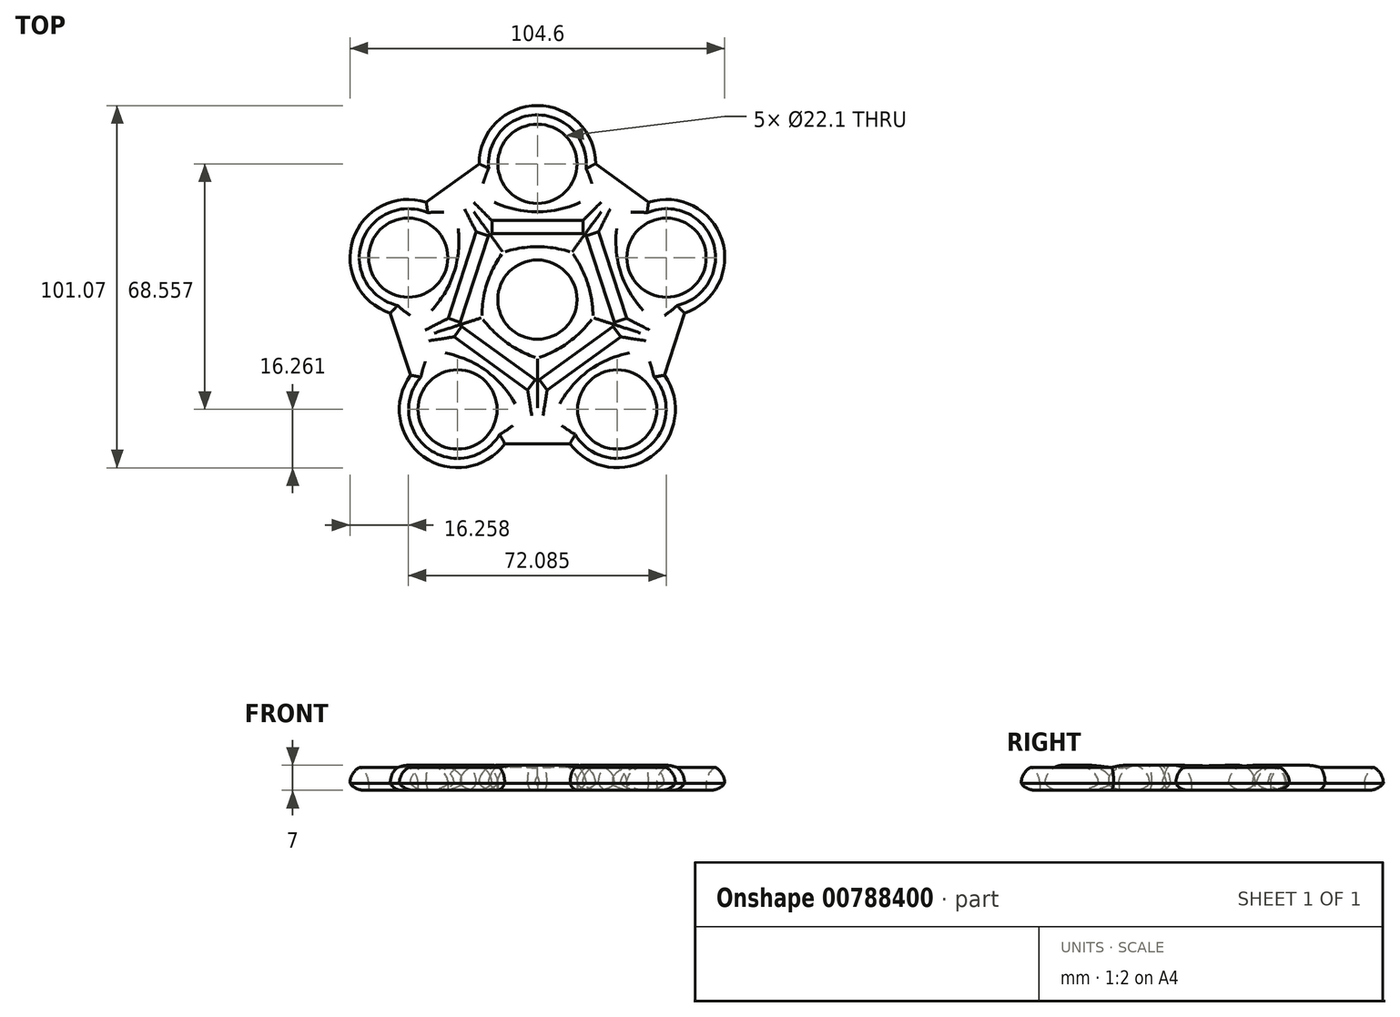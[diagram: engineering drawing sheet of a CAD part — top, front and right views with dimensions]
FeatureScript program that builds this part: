
annotation { "Feature Type Name" : "Feature", "Feature Type Description" : "" }
export const myFeature = defineFeature(function(context is Context, id is Id, definition is map)
    precondition{}
    {
        {
            var Q0;
            Q0=qCreatedBy(makeId("Top.planeOp"),FACE);
            var sketch = newSketch(context, id + "F0", { "sketchPlane" : qUnion([Q0])});
            skCircle(sketch, "E0", {"center": v(0, 0) * mm, "radius": 11.05 * mm});
            skCircle(sketch, "E1", {"center": v(0, 37.9) * mm, "radius": 11.05 * mm});
            skCircle(sketch, "E2.1.0", {"center": v(-36.04, 11.71) * mm, "radius": 11.05 * mm});
            skCircle(sketch, "E2.2.0", {"center": v(-22.28, -30.66) * mm, "radius": 11.05 * mm});
            skCircle(sketch, "E2.3.0", {"center": v(22.28, -30.66) * mm, "radius": 11.05 * mm});
            skCircle(sketch, "E2.4.0", {"center": v(36.04, 11.71) * mm, "radius": 11.05 * mm});
            skLineSegment(sketch, "E3", {"start": v(0, 37.9) * mm, "end": v(16.26, 37.9) * mm, "construction": true});
            skLineSegment(sketch, "E4", {"start": v(-16.26, 37.9) * mm, "end": v(-16.26, 37.9) * mm});
            skArc(sketch, "E5", {"start": v(16.26, 37.9) * mm, "mid": v(0, 54.15) * mm, "end": v(-16.26, 37.9) * mm});
            skArc(sketch, "E6.1.0", {"start": v(-31.02, 27.17) * mm, "mid": v(-51.5, 16.73) * mm, "end": v(-41.07, -3.75) * mm});
            skArc(sketch, "E6.2.0", {"start": v(-35.43, -21.1) * mm, "mid": v(-31.83, -43.81) * mm, "end": v(-9.12, -40.21) * mm});
            skArc(sketch, "E6.3.0", {"start": v(9.12, -40.21) * mm, "mid": v(31.83, -43.81) * mm, "end": v(35.43, -21.1) * mm});
            skArc(sketch, "E6.4.0", {"start": v(41.07, -3.75) * mm, "mid": v(51.5, 16.73) * mm, "end": v(31.02, 27.17) * mm});
            skLineSegment(sketch, "E7", {"start": v(-16.26, 37.9) * mm, "end": v(-31.02, 27.17) * mm});
            skLineSegment(sketch, "E8.1.0", {"start": v(-41.07, -3.75) * mm, "end": v(-35.43, -21.1) * mm});
            skLineSegment(sketch, "E8.2.0", {"start": v(-9.12, -40.21) * mm, "end": v(9.12, -40.21) * mm});
            skLineSegment(sketch, "E8.3.0", {"start": v(35.43, -21.1) * mm, "end": v(41.07, -3.75) * mm});
            skLineSegment(sketch, "E8.4.0", {"start": v(31.02, 27.17) * mm, "end": v(16.26, 37.9) * mm});
            skLineSegment(sketch, "E9.bottom", {"start": v(12.7, 18.46) * mm, "end": v(-12.7, 18.46) * mm});
            skLineSegment(sketch, "E9.top", {"start": v(12.7, 22.06) * mm, "end": v(-12.7, 22.06) * mm});
            skLineSegment(sketch, "E9.left", {"start": v(12.7, 18.46) * mm, "end": v(12.7, 22.06) * mm});
            skLineSegment(sketch, "E9.right", {"start": v(-12.7, 18.46) * mm, "end": v(-12.7, 22.06) * mm});
            skPoint(sketch, "E9.middle", {"position": v(0, 20.26) * mm});
            skLineSegment(sketch, "E10.1.0", {"start": v(-13.63, 17.77) * mm, "end": v(-17.06, 18.89) * mm});
            skLineSegment(sketch, "E10.1.1", {"start": v(-17.06, 18.89) * mm, "end": v(-24.9, -5.25) * mm});
            skLineSegment(sketch, "E10.1.2", {"start": v(-13.63, 17.77) * mm, "end": v(-21.48, -6.37) * mm});
            skLineSegment(sketch, "E10.1.3", {"start": v(-21.48, -6.37) * mm, "end": v(-24.9, -5.25) * mm});
            skPoint(sketch, "E10.1.4", {"position": v(-19.27, 6.26) * mm});
            skLineSegment(sketch, "E10.2.0", {"start": v(-21.12, -7.47) * mm, "end": v(-23.23, -10.39) * mm});
            skLineSegment(sketch, "E10.2.1", {"start": v(-23.23, -10.39) * mm, "end": v(-2.7, -25.3) * mm});
            skLineSegment(sketch, "E10.2.2", {"start": v(-21.12, -7.47) * mm, "end": v(-0.58, -22.4) * mm});
            skLineSegment(sketch, "E10.2.3", {"start": v(-0.58, -22.4) * mm, "end": v(-2.7, -25.3) * mm});
            skPoint(sketch, "E10.2.4", {"position": v(-11.9, -16.4) * mm});
            skLineSegment(sketch, "E10.3.0", {"start": v(0.58, -22.4) * mm, "end": v(2.7, -25.3) * mm});
            skLineSegment(sketch, "E10.3.1", {"start": v(2.7, -25.3) * mm, "end": v(23.23, -10.39) * mm});
            skLineSegment(sketch, "E10.3.2", {"start": v(0.58, -22.4) * mm, "end": v(21.12, -7.47) * mm});
            skLineSegment(sketch, "E10.3.3", {"start": v(21.12, -7.47) * mm, "end": v(23.23, -10.39) * mm});
            skPoint(sketch, "E10.3.4", {"position": v(11.9, -16.4) * mm});
            skLineSegment(sketch, "E10.4.0", {"start": v(21.48, -6.37) * mm, "end": v(24.9, -5.25) * mm});
            skLineSegment(sketch, "E10.4.1", {"start": v(24.9, -5.25) * mm, "end": v(17.06, 18.89) * mm});
            skLineSegment(sketch, "E10.4.2", {"start": v(21.48, -6.37) * mm, "end": v(13.63, 17.77) * mm});
            skLineSegment(sketch, "E10.4.3", {"start": v(13.63, 17.77) * mm, "end": v(17.06, 18.89) * mm});
            skPoint(sketch, "E10.4.4", {"position": v(19.27, 6.26) * mm});
            skSolve(sketch);
        }
        {
            var Q0;
            Q0 = qSketchRegion(id + "F0", true);
            extrude(context, id + "F1", {"entities" : qUnion([Q0]), "depth" : 7 * mm, "offsetDistance" : 25.4 * mm});
        }
        {
            var Q0;
            Q0=makeQuery(id+"F1.opExtrude","CAP_EDGE",EDGE,{"disambiguationData":[OSD([sQuery(id+"F0.wireOp",EDGE,"E7")])],"isStart":false});
            var Q1;
            Q1=makeQuery(id+"F1.opExtrude","CAP_EDGE",EDGE,{"disambiguationData":[OSD([sQuery(id+"F0.wireOp",EDGE,"E6.1.0")])],"isStart":false});
            var Q2;
            Q2=makeQuery(id+"F1.opExtrude","CAP_EDGE",EDGE,{"disambiguationData":[OSD([sQuery(id+"F0.wireOp",EDGE,"E8.1.0")])],"isStart":false});
            var Q3;
            Q3=makeQuery(id+"F1.opExtrude","CAP_EDGE",EDGE,{"disambiguationData":[OSD([sQuery(id+"F0.wireOp",EDGE,"E6.2.0")])],"isStart":false});
            var Q4;
            Q4=makeQuery(id+"F1.opExtrude","CAP_EDGE",EDGE,{"disambiguationData":[OSD([sQuery(id+"F0.wireOp",EDGE,"E8.2.0")])],"isStart":false});
            var Q5;
            Q5=makeQuery(id+"F1.opExtrude","CAP_EDGE",EDGE,{"disambiguationData":[OSD([sQuery(id+"F0.wireOp",EDGE,"E6.3.0")])],"isStart":false});
            var Q6;
            Q6=makeQuery(id+"F1.opExtrude","CAP_EDGE",EDGE,{"disambiguationData":[OSD([sQuery(id+"F0.wireOp",EDGE,"E8.3.0")])],"isStart":false});
            var Q7;
            Q7=makeQuery(id+"F1.opExtrude","CAP_EDGE",EDGE,{"disambiguationData":[OSD([sQuery(id+"F0.wireOp",EDGE,"E6.4.0")])],"isStart":false});
            var Q8;
            Q8=makeQuery(id+"F1.opExtrude","CAP_EDGE",EDGE,{"disambiguationData":[OSD([sQuery(id+"F0.wireOp",EDGE,"E8.4.0")])],"isStart":false});
            var Q9;
            Q9=makeQuery(id+"F1.opExtrude","CAP_EDGE",EDGE,{"disambiguationData":[OSD([sQuery(id+"F0.wireOp",EDGE,"E5")])],"isStart":false});
            var Q10;
            Q10=makeQuery(id+"F1.opExtrude","CAP_EDGE",EDGE,{"disambiguationData":[OSD([sQuery(id+"F0.wireOp",EDGE,"E9.bottom")])],"isStart":false});
            var Q11;
            Q11=makeQuery(id+"F1.opExtrude","CAP_EDGE",EDGE,{"disambiguationData":[OSD([sQuery(id+"F0.wireOp",EDGE,"E9.top")])],"isStart":false});
            var Q12;
            Q12=makeQuery(id+"F1.opExtrude","CAP_EDGE",EDGE,{"disambiguationData":[OSD([sQuery(id+"F0.wireOp",EDGE,"E9.right")])],"isStart":false});
            var Q13;
            Q13=makeQuery(id+"F1.opExtrude","CAP_EDGE",EDGE,{"disambiguationData":[OSD([sQuery(id+"F0.wireOp",EDGE,"E9.left")])],"isStart":false});
            var Q14;
            Q14=makeQuery(id+"F1.opExtrude","CAP_EDGE",EDGE,{"disambiguationData":[OSD([sQuery(id+"F0.wireOp",EDGE,"E10.4.2")])],"isStart":false});
            var Q15;
            Q15=makeQuery(id+"F1.opExtrude","CAP_EDGE",EDGE,{"disambiguationData":[OSD([sQuery(id+"F0.wireOp",EDGE,"E10.4.3")])],"isStart":false});
            var Q16;
            Q16=makeQuery(id+"F1.opExtrude","CAP_EDGE",EDGE,{"disambiguationData":[OSD([sQuery(id+"F0.wireOp",EDGE,"E10.4.1")])],"isStart":false});
            var Q17;
            Q17=makeQuery(id+"F1.opExtrude","CAP_EDGE",EDGE,{"disambiguationData":[OSD([sQuery(id+"F0.wireOp",EDGE,"E10.4.0")])],"isStart":false});
            var Q18;
            Q18=makeQuery(id+"F1.opExtrude","CAP_EDGE",EDGE,{"disambiguationData":[OSD([sQuery(id+"F0.wireOp",EDGE,"E10.3.1")])],"isStart":false});
            var Q19;
            Q19=makeQuery(id+"F1.opExtrude","CAP_EDGE",EDGE,{"disambiguationData":[OSD([sQuery(id+"F0.wireOp",EDGE,"E10.3.2")])],"isStart":false});
            var Q20;
            Q20=makeQuery(id+"F1.opExtrude","CAP_EDGE",EDGE,{"disambiguationData":[OSD([sQuery(id+"F0.wireOp",EDGE,"E10.3.3")])],"isStart":false});
            var Q21;
            Q21=makeQuery(id+"F1.opExtrude","CAP_EDGE",EDGE,{"disambiguationData":[OSD([sQuery(id+"F0.wireOp",EDGE,"E10.3.0")])],"isStart":false});
            var Q22;
            Q22=makeQuery(id+"F1.opExtrude","CAP_EDGE",EDGE,{"disambiguationData":[OSD([sQuery(id+"F0.wireOp",EDGE,"E10.2.2")])],"isStart":false});
            var Q23;
            Q23=makeQuery(id+"F1.opExtrude","CAP_EDGE",EDGE,{"disambiguationData":[OSD([sQuery(id+"F0.wireOp",EDGE,"E10.2.3")])],"isStart":false});
            var Q24;
            Q24=makeQuery(id+"F1.opExtrude","CAP_EDGE",EDGE,{"disambiguationData":[OSD([sQuery(id+"F0.wireOp",EDGE,"E10.2.1")])],"isStart":false});
            var Q25;
            Q25=makeQuery(id+"F1.opExtrude","CAP_EDGE",EDGE,{"disambiguationData":[OSD([sQuery(id+"F0.wireOp",EDGE,"E10.1.1")])],"isStart":false});
            var Q26;
            Q26=makeQuery(id+"F1.opExtrude","CAP_FACE",FACE,{"disambiguationData":[OSD([sQuery(id+"F0.wireOp",EDGE,"E0"),sQuery(id+"F0.wireOp",EDGE,"E1"),sQuery(id+"F0.wireOp",EDGE,"E2.1.0"),sQuery(id+"F0.wireOp",EDGE,"E2.2.0"),sQuery(id+"F0.wireOp",EDGE,"E2.3.0"),sQuery(id+"F0.wireOp",EDGE,"E2.4.0"),sQuery(id+"F0.wireOp",EDGE,"E5"),sQuery(id+"F0.wireOp",EDGE,"E6.1.0"),sQuery(id+"F0.wireOp",EDGE,"E6.2.0"),sQuery(id+"F0.wireOp",EDGE,"E6.3.0"),sQuery(id+"F0.wireOp",EDGE,"E6.4.0"),sQuery(id+"F0.wireOp",EDGE,"E7"),sQuery(id+"F0.wireOp",EDGE,"E8.1.0"),sQuery(id+"F0.wireOp",EDGE,"E8.2.0"),sQuery(id+"F0.wireOp",EDGE,"E8.3.0"),sQuery(id+"F0.wireOp",EDGE,"E8.4.0"),sQuery(id+"F0.wireOp",EDGE,"E9.bottom"),sQuery(id+"F0.wireOp",EDGE,"E9.top"),sQuery(id+"F0.wireOp",EDGE,"E9.left"),sQuery(id+"F0.wireOp",EDGE,"E9.right"),sQuery(id+"F0.wireOp",EDGE,"E10.1.0"),sQuery(id+"F0.wireOp",EDGE,"E10.1.1"),sQuery(id+"F0.wireOp",EDGE,"E10.1.2"),sQuery(id+"F0.wireOp",EDGE,"E10.1.3"),sQuery(id+"F0.wireOp",EDGE,"E10.2.0"),sQuery(id+"F0.wireOp",EDGE,"E10.2.1"),sQuery(id+"F0.wireOp",EDGE,"E10.2.2"),sQuery(id+"F0.wireOp",EDGE,"E10.2.3"),sQuery(id+"F0.wireOp",EDGE,"E10.3.0"),sQuery(id+"F0.wireOp",EDGE,"E10.3.1"),sQuery(id+"F0.wireOp",EDGE,"E10.3.2"),sQuery(id+"F0.wireOp",EDGE,"E10.3.3"),sQuery(id+"F0.wireOp",EDGE,"E10.4.0"),sQuery(id+"F0.wireOp",EDGE,"E10.4.1"),sQuery(id+"F0.wireOp",EDGE,"E10.4.2"),sQuery(id+"F0.wireOp",EDGE,"E10.4.3")])],"isStart":false});
            var Q27;
            Q27=makeQuery(id+"F1.opExtrude","CAP_EDGE",EDGE,{"disambiguationData":[OSD([sQuery(id+"F0.wireOp",EDGE,"E10.1.3")])],"isStart":false});
            var Q28;
            Q28=makeQuery(id+"F1.opExtrude","CAP_EDGE",EDGE,{"disambiguationData":[OSD([sQuery(id+"F0.wireOp",EDGE,"E10.1.0")])],"isStart":false});
            fillet(context, id + "F2", {"entities" : qUnion([Q0, Q1, Q2, Q3, Q4, Q5, Q6, Q7, Q8, Q9, Q10, Q11, Q12, Q13, Q14, Q15, Q16, Q17, Q18, Q19, Q20, Q21, Q22, Q23, Q24, Q25, Q26, Q27, Q28]), "radius" : 5.08 * mm, "tangentPropagation" : true, "allowEdgeOverflow" : false});
        }
        {
            var Q0;
            Q0=makeQuery(id+"F1.opExtrude","CAP_EDGE",EDGE,{"disambiguationData":[OSD([sQuery(id+"F0.wireOp",EDGE,"E10.4.1")])],"isStart":true});
            var Q1;
            Q1=makeQuery(id+"F1.opExtrude","CAP_EDGE",EDGE,{"disambiguationData":[OSD([sQuery(id+"F0.wireOp",EDGE,"E10.4.3")])],"isStart":true});
            var Q2;
            Q2=makeQuery(id+"F1.opExtrude","CAP_EDGE",EDGE,{"disambiguationData":[OSD([sQuery(id+"F0.wireOp",EDGE,"E10.3.1")])],"isStart":true});
            var Q3;
            Q3=makeQuery(id+"F1.opExtrude","CAP_EDGE",EDGE,{"disambiguationData":[OSD([sQuery(id+"F0.wireOp",EDGE,"E10.4.2")])],"isStart":true});
            var Q4;
            Q4=makeQuery(id+"F1.opExtrude","CAP_EDGE",EDGE,{"disambiguationData":[OSD([sQuery(id+"F0.wireOp",EDGE,"E10.4.0")])],"isStart":true});
            var Q5;
            Q5=makeQuery(id+"F1.opExtrude","CAP_EDGE",EDGE,{"disambiguationData":[OSD([sQuery(id+"F0.wireOp",EDGE,"E10.3.0")])],"isStart":true});
            var Q6;
            Q6=makeQuery(id+"F1.opExtrude","CAP_EDGE",EDGE,{"disambiguationData":[OSD([sQuery(id+"F0.wireOp",EDGE,"E10.3.2")])],"isStart":true});
            var Q7;
            Q7=makeQuery(id+"F1.opExtrude","CAP_EDGE",EDGE,{"disambiguationData":[OSD([sQuery(id+"F0.wireOp",EDGE,"E10.3.3")])],"isStart":true});
            var Q8;
            Q8=makeQuery(id+"F1.opExtrude","CAP_EDGE",EDGE,{"disambiguationData":[OSD([sQuery(id+"F0.wireOp",EDGE,"E10.2.1")])],"isStart":true});
            var Q9;
            Q9=makeQuery(id+"F1.opExtrude","CAP_EDGE",EDGE,{"disambiguationData":[OSD([sQuery(id+"F0.wireOp",EDGE,"E10.2.2")])],"isStart":true});
            var Q10;
            Q10=makeQuery(id+"F1.opExtrude","CAP_EDGE",EDGE,{"disambiguationData":[OSD([sQuery(id+"F0.wireOp",EDGE,"E10.2.3")])],"isStart":true});
            var Q11;
            Q11=makeQuery(id+"F1.opExtrude","CAP_EDGE",EDGE,{"disambiguationData":[OSD([sQuery(id+"F0.wireOp",EDGE,"E10.2.0")])],"isStart":true});
            var Q12;
            Q12=makeQuery(id+"F1.opExtrude","CAP_EDGE",EDGE,{"disambiguationData":[OSD([sQuery(id+"F0.wireOp",EDGE,"E10.1.2")])],"isStart":true});
            var Q13;
            Q13=makeQuery(id+"F1.opExtrude","CAP_EDGE",EDGE,{"disambiguationData":[OSD([sQuery(id+"F0.wireOp",EDGE,"E10.1.1")])],"isStart":true});
            var Q14;
            Q14=makeQuery(id+"F1.opExtrude","CAP_EDGE",EDGE,{"disambiguationData":[OSD([sQuery(id+"F0.wireOp",EDGE,"E10.1.0")])],"isStart":true});
            var Q15;
            Q15=makeQuery(id+"F1.opExtrude","CAP_EDGE",EDGE,{"disambiguationData":[OSD([sQuery(id+"F0.wireOp",EDGE,"E10.1.3")])],"isStart":true});
            var Q16;
            Q16=makeQuery(id+"F1.opExtrude","CAP_EDGE",EDGE,{"disambiguationData":[OSD([sQuery(id+"F0.wireOp",EDGE,"E9.bottom")])],"isStart":true});
            var Q17;
            Q17=makeQuery(id+"F1.opExtrude","CAP_EDGE",EDGE,{"disambiguationData":[OSD([sQuery(id+"F0.wireOp",EDGE,"E9.left")])],"isStart":true});
            var Q18;
            Q18=makeQuery(id+"F1.opExtrude","CAP_EDGE",EDGE,{"disambiguationData":[OSD([sQuery(id+"F0.wireOp",EDGE,"E9.top")])],"isStart":true});
            var Q19;
            Q19=makeQuery(id+"F1.opExtrude","CAP_EDGE",EDGE,{"disambiguationData":[OSD([sQuery(id+"F0.wireOp",EDGE,"E9.right")])],"isStart":true});
            var Q20;
            Q20=makeQuery(id+"F1.opExtrude","CAP_EDGE",EDGE,{"disambiguationData":[OSD([sQuery(id+"F0.wireOp",EDGE,"E7")])],"isStart":true});
            var Q21;
            Q21=makeQuery(id+"F1.opExtrude","CAP_EDGE",EDGE,{"disambiguationData":[OSD([sQuery(id+"F0.wireOp",EDGE,"E5")])],"isStart":true});
            var Q22;
            Q22=makeQuery(id+"F1.opExtrude","CAP_EDGE",EDGE,{"disambiguationData":[OSD([sQuery(id+"F0.wireOp",EDGE,"E8.4.0")])],"isStart":true});
            var Q23;
            Q23=makeQuery(id+"F1.opExtrude","CAP_EDGE",EDGE,{"disambiguationData":[OSD([sQuery(id+"F0.wireOp",EDGE,"E6.4.0")])],"isStart":true});
            var Q24;
            Q24=makeQuery(id+"F1.opExtrude","CAP_EDGE",EDGE,{"disambiguationData":[OSD([sQuery(id+"F0.wireOp",EDGE,"E8.3.0")])],"isStart":true});
            var Q25;
            Q25=makeQuery(id+"F1.opExtrude","CAP_EDGE",EDGE,{"disambiguationData":[OSD([sQuery(id+"F0.wireOp",EDGE,"E6.3.0")])],"isStart":true});
            var Q26;
            Q26=makeQuery(id+"F1.opExtrude","CAP_EDGE",EDGE,{"disambiguationData":[OSD([sQuery(id+"F0.wireOp",EDGE,"E8.2.0")])],"isStart":true});
            var Q27;
            Q27=makeQuery(id+"F1.opExtrude","CAP_EDGE",EDGE,{"disambiguationData":[OSD([sQuery(id+"F0.wireOp",EDGE,"E6.2.0")])],"isStart":true});
            var Q28;
            Q28=makeQuery(id+"F1.opExtrude","CAP_EDGE",EDGE,{"disambiguationData":[OSD([sQuery(id+"F0.wireOp",EDGE,"E8.1.0")])],"isStart":true});
            var Q29;
            Q29=makeQuery(id+"F1.opExtrude","CAP_EDGE",EDGE,{"disambiguationData":[OSD([sQuery(id+"F0.wireOp",EDGE,"E6.1.0")])],"isStart":true});
            fillet(context, id + "F3", {"entities" : qUnion([Q0, Q1, Q2, Q3, Q4, Q5, Q6, Q7, Q8, Q9, Q10, Q11, Q12, Q13, Q14, Q15, Q16, Q17, Q18, Q19, Q20, Q21, Q22, Q23, Q24, Q25, Q26, Q27, Q28, Q29]), "radius" : 5.08 * mm, "tangentPropagation" : true, "allowEdgeOverflow" : false});
        }
        {
            var Q0;
            Q0=makeQuery(id+"F1.opExtrude","CAP_EDGE",EDGE,{"disambiguationData":[OSD([sQuery(id+"F0.wireOp",EDGE,"E0")])],"isStart":true});
            fillet(context, id + "F4", {"entities" : qUnion([Q0]), "radius" : 5.08 * mm, "tangentPropagation" : true, "allowEdgeOverflow" : false});
        }
    });
